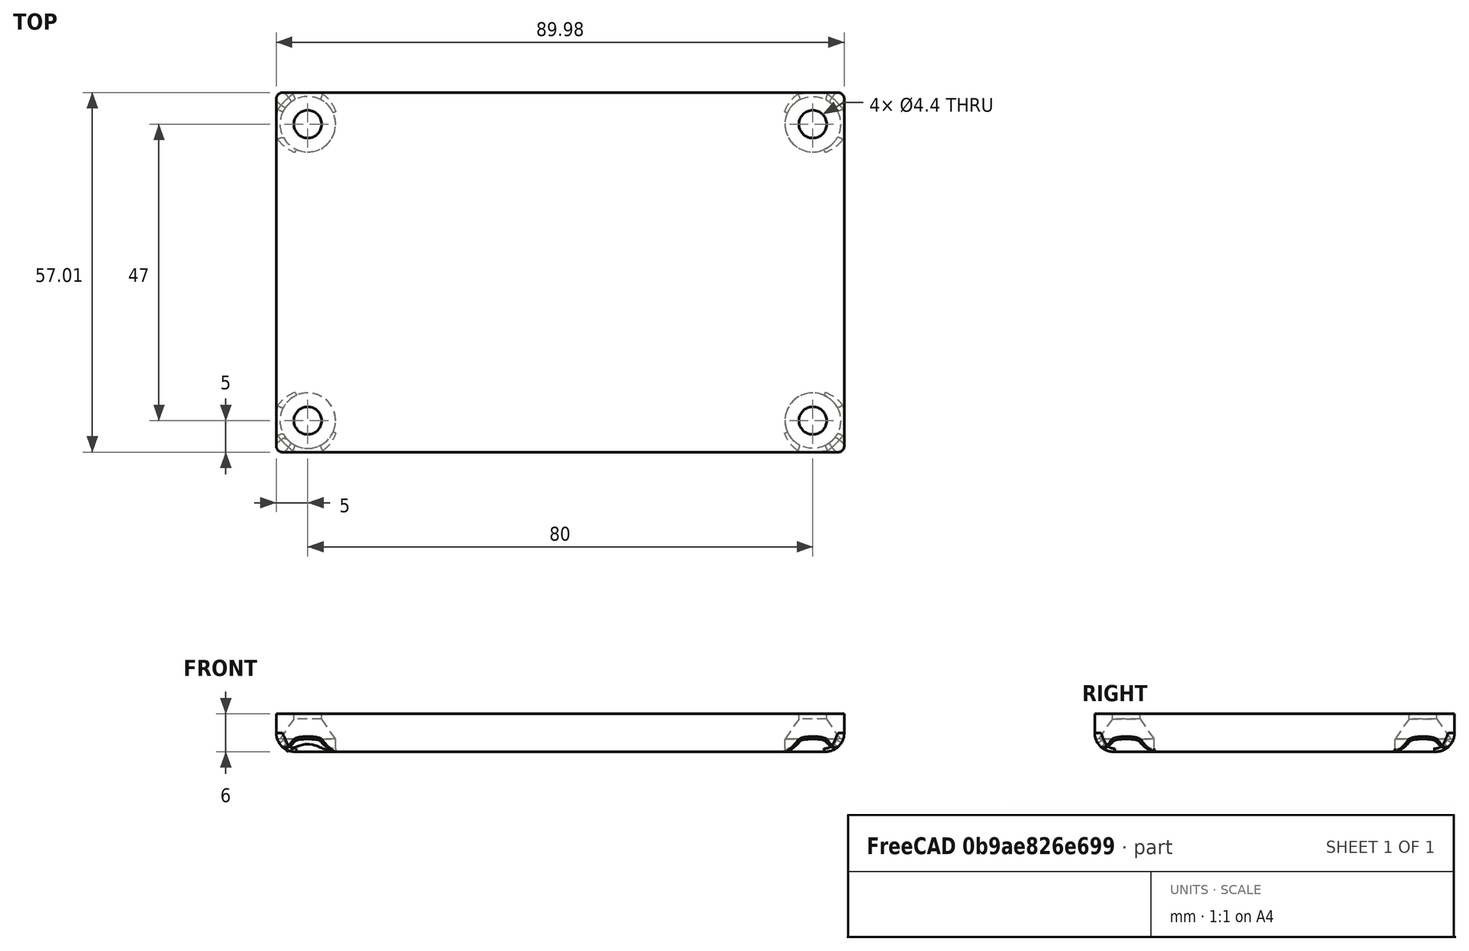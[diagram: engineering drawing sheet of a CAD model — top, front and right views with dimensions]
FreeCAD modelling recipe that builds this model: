
FCSTD DOCUMENT  (FreeCAD 0.16R)
Label: BoxBeltClipGateway
License: All rights reserved
LicenseURL: http://en.wikipedia.org/wiki/All_rights_reserved
objects: Part::MultiFuse×9, Part::Cylinder×8, Part::Cone×4, Part::Fillet×2, Sketcher::SketchObject×1, PartDesign::Pad×1, Part::Cut×1
note: 27 computed .brp shape members not serialized (recipe doc carries the construction recipe); baked Part::Feature solids carry a one-line shape summary decoded from their .brp

FEATURE [Sketcher::SketchObject] Sketch002
  sketch-geometry (8):
    g0: LineSegment StartX=16.0115 StartY=-28 StartZ=0 EndX=-72 EndY=-28 EndZ=0
    g1: LineSegment StartX=-73.0008 StartY=-26.9992 StartZ=0 EndX=-73.0008 EndY=28.0015 EndZ=0
    g2: LineSegment StartX=-71.9972 StartY=29.005 StartZ=0 EndX=15.9984 EndY=29.005 EndZ=0
    g3: LineSegment StartX=16.9833 StartY=28.0201 StartZ=0 EndX=16.9833 EndY=-27.0282 EndZ=0
    g4: ArcOfCircle CenterX=16.0115 CenterY=-27.0282 CenterZ=0 NormalX=0 NormalY=0 NormalZ=1 Radius=0.97176 StartAngle=4.71239 EndAngle=6.28319
    g5: ArcOfCircle CenterX=-72 CenterY=-26.9992 CenterZ=0 NormalX=0 NormalY=0 NormalZ=1 Radius=1.00077 StartAngle=3.14159 EndAngle=4.71239
    g6: ArcOfCircle CenterX=-71.9972 CenterY=28.0015 CenterZ=0 NormalX=0 NormalY=0 NormalZ=1 Radius=1.00354 StartAngle=1.5708 EndAngle=3.14159
    g7: ArcOfCircle CenterX=15.9984 CenterY=28.0201 CenterZ=0 NormalX=0 NormalY=0 NormalZ=1 Radius=0.984903 StartAngle=0 EndAngle=1.5708
  constraints (12):
    c: Horizontal(g0)
    c: Horizontal(g2)
    c: Vertical(g1)
    c: Vertical(g3)
    c: Tangent(g3,g4) = 1.5708
    c: Tangent(g0,g4) = 1.5708
    c: Tangent(g1,g5) = 1.5708
    c: Tangent(g0,g5) = 1.5708
    c: Tangent(g1,g6) = 1.5708
    c: Tangent(g2,g6) = 1.5708
    c: Tangent(g2,g7) = 1.5708
    c: Tangent(g3,g7) = 1.5708
FEATURE [PartDesign::Pad] Pad013
  Length = 6
  Length2 = 100
  Sketch = -> Sketch002
  Type = 0
FEATURE [Part::Cylinder] Cylinder005  label="Zylinder"
  Angle = 360
  Height = 16
  Placement = pos=(12,-23,-1) rot=(0,0,1;0rad)
  Radius = 2.2
FEATURE [Part::Cone] Cone  label="Kegel"
  Angle = 360
  Height = 3.2
  Placement = pos=(12,-23,-1) rot=(0,0,1;0rad)
  Radius1 = 4.4
  Radius2 = 2.2
FEATURE [Part::MultiFuse] Fusion002  label="Bohrung001"
  Shapes = -> [Cylinder005,Cone]
FEATURE [Part::Cylinder] Cylinder006  label="Zylinder003"
  Angle = 360
  Height = 16
  Placement = pos=(12,-23,-1) rot=(0,0,1;0rad)
  Radius = 2.2
FEATURE [Part::Cone] Cone001  label="Kegel001"
  Angle = 360
  Height = 3.2
  Placement = pos=(12,-23,-1) rot=(0,0,1;0rad)
  Radius1 = 4.4
  Radius2 = 2.2
FEATURE [Part::MultiFuse] Fusion003  label="Bohrung002"
  Placement = pos=(0,47,0) rot=(0,0,1;0rad)
  Shapes = -> [Cylinder006,Cone001]
FEATURE [Part::Cylinder] Cylinder007  label="Zylinder004"
  Angle = 360
  Height = 16
  Placement = pos=(12,-23,-1) rot=(0,0,1;0rad)
  Radius = 2.2
FEATURE [Part::Cone] Cone002  label="Kegel002"
  Angle = 360
  Height = 3.2
  Placement = pos=(12,-23,-1) rot=(0,0,1;0rad)
  Radius1 = 4.4
  Radius2 = 2.2
FEATURE [Part::MultiFuse] Fusion004  label="Bohrung003"
  Placement = pos=(-80,0,1) rot=(0,0,1;0rad)
  Shapes = -> [Cylinder007,Cone002]
FEATURE [Part::Cylinder] Cylinder008  label="Zylinder005"
  Angle = 360
  Height = 16
  Placement = pos=(12,-23,-1) rot=(0,0,1;0rad)
  Radius = 2.2
FEATURE [Part::Cone] Cone003  label="Kegel003"
  Angle = 360
  Height = 3.2
  Placement = pos=(12,-23,-1) rot=(0,0,1;0rad)
  Radius1 = 4.4
  Radius2 = 2.2
FEATURE [Part::MultiFuse] Fusion005  label="Bohrung004"
  Placement = pos=(-80,47,0) rot=(0,0,1;0rad)
  Shapes = -> [Cylinder008,Cone003]
FEATURE [Part::Fillet] Fillet
  Base = -> Pad013
  Edges = 1 edges r=3: [Edge21]
FEATURE [Part::Cylinder] Cylinder  label="Zylinder006"
  Angle = 360
  Height = 3
  Placement = pos=(12,24,-4) rot=(0,0,1;0rad)
  Radius = 4.4
FEATURE [Part::MultiFuse] Fusion
  Placement = pos=(0,0,3) rot=(0,0,1;0rad)
  Shapes = -> [Cylinder,Fusion003]
FEATURE [Part::Cylinder] Cylinder009  label="Zylinder007"
  Angle = 360
  Height = 3
  Placement = pos=(-68,24,-4) rot=(0,0,1;0rad)
  Radius = 4.4
FEATURE [Part::Cylinder] Cylinder010  label="Zylinder008"
  Angle = 360
  Height = 3
  Placement = pos=(12,-23,-4) rot=(0,0,1;0rad)
  Radius = 4.4
FEATURE [Part::Cylinder] Cylinder011  label="Zylinder009"
  Angle = 360
  Height = 3
  Placement = pos=(-68,-23,-3) rot=(0,0,1;0rad)
  Radius = 4.4
FEATURE [Part::MultiFuse] Fusion006
  Placement = pos=(0,0,3) rot=(0,0,1;0rad)
  Shapes = -> [Fusion005,Cylinder009]
FEATURE [Part::MultiFuse] Fusion007
  Placement = pos=(0,0,2) rot=(0,0,1;0rad)
  Shapes = -> [Fusion004,Cylinder011]
FEATURE [Part::MultiFuse] Fusion008
  Placement = pos=(0,0,3) rot=(0,0,1;0rad)
  Shapes = -> [Fusion002,Cylinder010]
FEATURE [Part::MultiFuse] Fusion009  label="Bohrungen"
  Shapes = -> [Fusion,Fusion006,Fusion008,Fusion007]
FEATURE [Part::Cut] Cut
  Base = -> Fillet
  Tool = -> Fusion009
FEATURE [Part::Fillet] Fillet001
  Base = -> Cut
  Edges = 20 edges r=0.5: [Edge9,Edge10,Edge12,Edge13,Edge28,Edge31,Edge33,Edge34,Edge37,Edge38,Edge40,Edge41,Edge43,Edge45,Edge63,Edge66,Edge68,Edge69,Edge73,Edge75]
